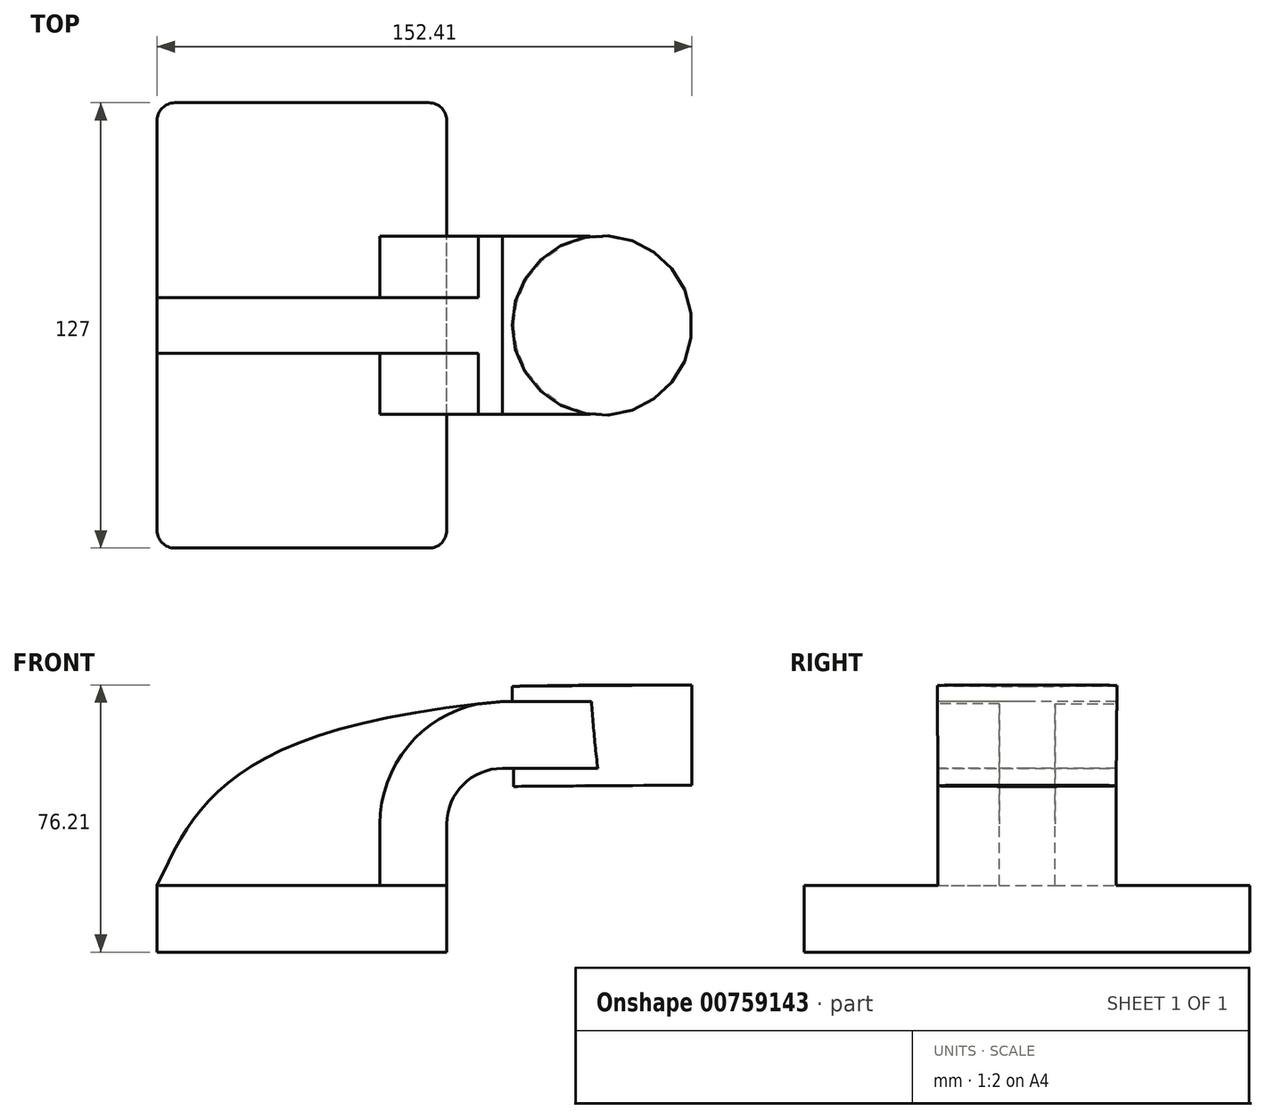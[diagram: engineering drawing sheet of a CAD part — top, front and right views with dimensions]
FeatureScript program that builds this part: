
annotation { "Feature Type Name" : "Feature", "Feature Type Description" : "" }
export const myFeature = defineFeature(function(context is Context, id is Id, definition is map)
    precondition{}
    {
        {
            var Q0;
            Q0=qCreatedBy(makeId("Front.planeOp"),FACE);
            var sketch = newSketch(context, id + "F0", { "sketchPlane" : qUnion([Q0])});
            skLineSegment(sketch, "E0.bottom", {"start": v(-41.27, -9.53) * mm, "end": v(41.28, -9.53) * mm});
            skLineSegment(sketch, "E0.top", {"start": v(-41.28, 9.53) * mm, "end": v(41.28, 9.53) * mm});
            skLineSegment(sketch, "E0.left", {"start": v(-41.28, -9.53) * mm, "end": v(-41.28, 9.53) * mm});
            skLineSegment(sketch, "E0.right", {"start": v(41.28, -9.53) * mm, "end": v(41.28, 9.52) * mm});
            skPoint(sketch, "E0.middle", {"position": v(0, 0) * mm});
            skLineSegment(sketch, "E1.bottom", {"start": v(60.32, 38.1) * mm, "end": v(111.12, 38.1) * mm});
            skLineSegment(sketch, "E1.top", {"start": v(60.32, 66.67) * mm, "end": v(111.12, 66.67) * mm});
            skLineSegment(sketch, "E1.left", {"start": v(60.32, 38.1) * mm, "end": v(60.32, 66.67) * mm});
            skLineSegment(sketch, "E1.right", {"start": v(111.12, 38.1) * mm, "end": v(111.12, 66.67) * mm});
            skPoint(sketch, "E1.middle", {"position": v(85.72, 52.39) * mm});
            skLineSegment(sketch, "E2", {"start": v(41.28, 9.52) * mm, "end": v(41.28, 27) * mm});
            skArc(sketch, "E3", {"start": v(57.15, 42.88) * mm, "mid": v(45.92, 38.23) * mm, "end": v(41.27, 27) * mm});
            skLineSegment(sketch, "E4", {"start": v(57.15, 42.88) * mm, "end": v(85.7, 42.88) * mm});
            skLineSegment(sketch, "E5.0", {"start": v(57.15, 61.93) * mm, "end": v(85.5, 61.93) * mm});
            skArc(sketch, "E5.1", {"start": v(57.15, 61.93) * mm, "mid": v(32.45, 51.7) * mm, "end": v(22.22, 27) * mm});
            skLineSegment(sketch, "E5.2", {"start": v(22.22, 9.52) * mm, "end": v(22.22, 27) * mm});
            skLineSegment(sketch, "E6", {"start": v(85.72, 38.1) * mm, "end": v(85.5, 66.67) * mm});
            skFitSpline(sketch, "E7", {"points": [v(-41.28, 9.53) * mm, v(57.15, 61.93) * mm], "startDerivative": vector(30.95, 62.36) * mm, "endDerivative": vector(242.22, 21.98) * mm});
            skSolve(sketch);
        }
        {
            var Q0;
            Q0=makeQuery(id+"F0.imprint","IMPRINT",FACE,{"disambiguationData":[TD([[makeQuery(id+"F0.imprint","IMPRINT",EDGE,{"derivedFrom":sQuery(id+"F0.wireOp",EDGE,"E0.bottom")}),1.0]])]});
            extrude(context, id + "F1", {"entities" : qUnion([Q0]), "endBound" : BoundingType.SYMMETRIC, "depth" : 127 * mm, "offsetDistance" : 25.4 * mm});
        }
        {
            var Q0;
            {var subQ1=sQuery(id+"F0.wireOp",EDGE,"E2");Q0=makeQuery(id+"F0.imprint","IMPRINT",FACE,{"disambiguationData":[TD([[makeQuery(id+"F0.imprint","IMPRINT",EDGE,{"derivedFrom":subQ1}),1.0]])]});}
            extrude(context, id + "F2", {"entities" : qUnion([Q0]), "operationType" : NewBodyOperationType.ADD, "endBound" : BoundingType.SYMMETRIC, "depth" : 50.8 * mm, "offsetDistance" : 25.4 * mm});
        }
        {
            var Q0;
            {var subQ0=sQuery(id+"F0.wireOp",EDGE,"E1.right");Q0=makeQuery(id+"F0.imprint","IMPRINT",FACE,{"disambiguationData":[TD([[makeQuery(id+"F0.imprint","IMPRINT",EDGE,{"derivedFrom":subQ0}),1.0]])]});}
            var Q1;
            Q1=sQuery(id+"F0.wireOp",EDGE,"E6");
            revolve(context, id + "F3", {"operationType" : NewBodyOperationType.ADD, "surfaceOperationType" : NewSurfaceOperationType.NEW, "entities" : qUnion([Q0]), "axis" : qUnion([Q1]), "revolveType" : RevolveType.FULL});
        }
        {
            var Q0;
            Q0=sQuery(id+"F0.wireOp",EDGE,"E5.0");
            var Q1;
            Q1=sQuery(id+"F0.wireOp",EDGE,"E4");
            extrude(context, id + "F4", {"bodyType" : ToolBodyType.SURFACE, "surfaceEntities" : qUnion([Q0, Q1]), "endBound" : BoundingType.SYMMETRIC, "depth" : 50.8 * mm, "offsetDistance" : 25.4 * mm});
        }
        {
            var Q0;
            Q0=makeQuery(id+"F4.opExtrude","SWEPT_FACE",FACE,{"disambiguationData":[OSD([sQuery(id+"F0.wireOp",EDGE,"E5.0")])]});
            extrude(context, id + "F5", {"entities" : qUnion([Q0]), "operationType" : NewBodyOperationType.ADD, "depth" : 19.05 * mm, "offsetDistance" : 25.4 * mm});
        }
        {
            var Q0;
            {var subQ3=sQuery(id+"F0.wireOp",EDGE,"E5.2");Q0=makeQuery(id+"F0.imprint","IMPRINT",FACE,{"disambiguationData":[TD([[makeQuery(id+"F0.imprint","IMPRINT",EDGE,{"derivedFrom":subQ3}),1.0]])]});}
            extrude(context, id + "F6", {"entities" : qUnion([Q0]), "operationType" : NewBodyOperationType.ADD, "endBound" : BoundingType.SYMMETRIC, "depth" : 15.88 * mm, "offsetDistance" : 25.4 * mm});
        }
        {
            var Q0;
            Q0=makeQuery(id+"F1.opExtrude","CAP_EDGE",EDGE,{"disambiguationData":[OSD([sQuery(id+"F0.wireOp",EDGE,"E0.right")])],"isStart":false});
            var Q1;
            Q1=makeQuery(id+"F1.opExtrude","CAP_EDGE",EDGE,{"disambiguationData":[OSD([sQuery(id+"F0.wireOp",EDGE,"E0.left")])],"isStart":false});
            var Q2;
            Q2=makeQuery(id+"F1.opExtrude","CAP_EDGE",EDGE,{"disambiguationData":[OSD([sQuery(id+"F0.wireOp",EDGE,"E0.left")])],"isStart":true});
            var Q3;
            Q3=makeQuery(id+"F1.opExtrude","CAP_EDGE",EDGE,{"disambiguationData":[OSD([sQuery(id+"F0.wireOp",EDGE,"E0.right")])],"isStart":true});
            fillet(context, id + "F7", {"entities" : qUnion([Q0, Q1, Q2, Q3]), "radius" : 5.08 * mm, "tangentPropagation" : true, "allowEdgeOverflow" : false});
        }
    });
